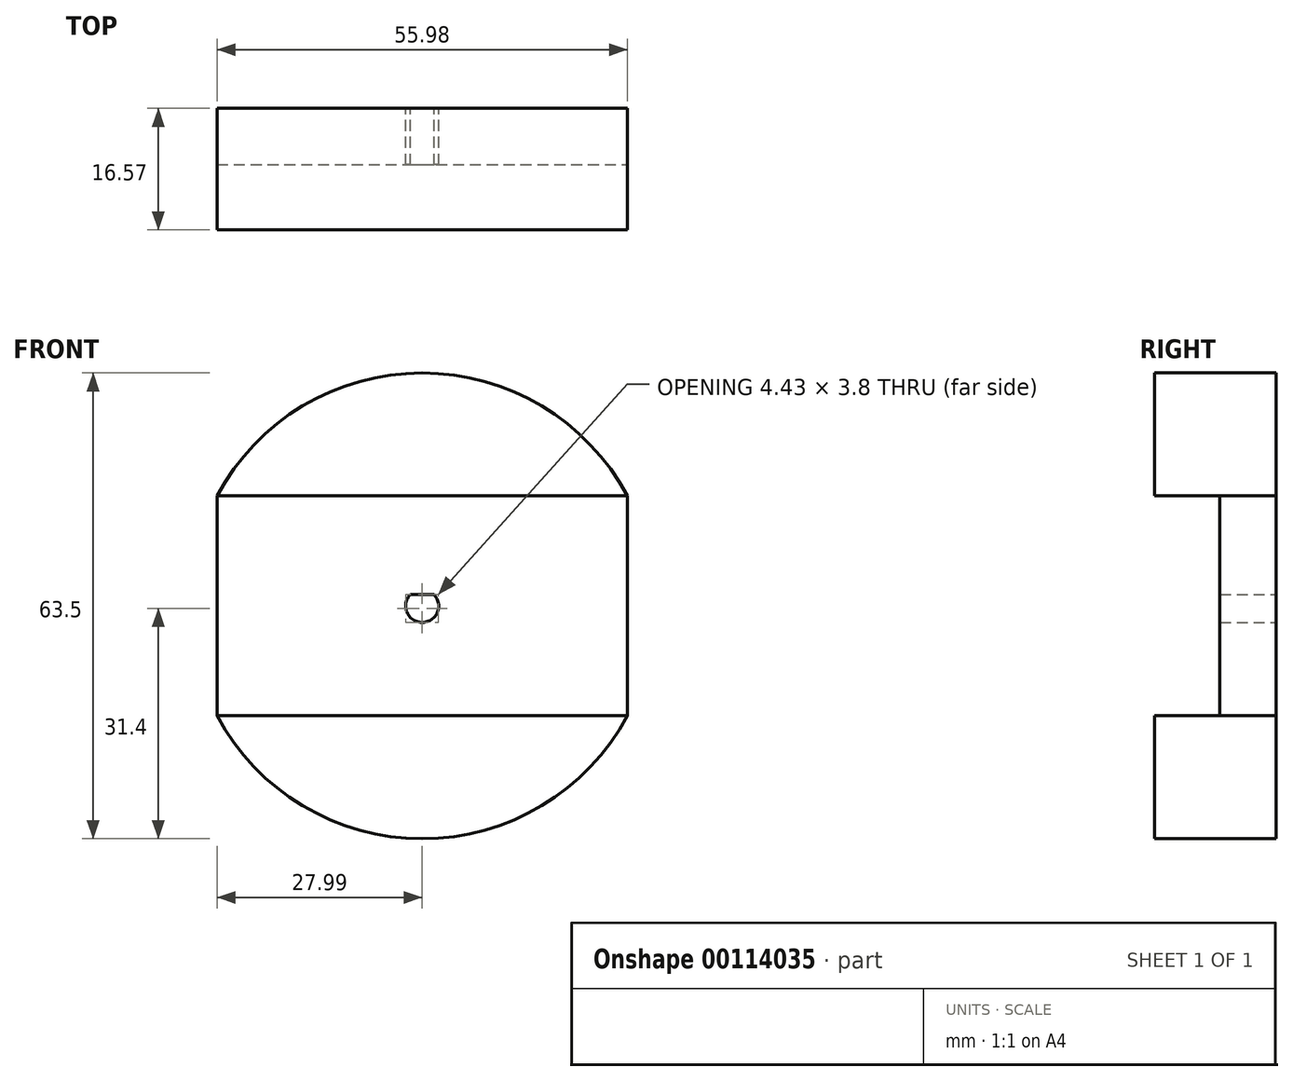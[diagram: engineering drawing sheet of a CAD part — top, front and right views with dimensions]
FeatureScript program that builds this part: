
annotation { "Feature Type Name" : "Feature", "Feature Type Description" : "" }
export const myFeature = defineFeature(function(context is Context, id is Id, definition is map)
    precondition{}
    {
        {
            var Q0;
            Q0=qCreatedBy(makeId("Front.planeOp"),FACE);
            var sketch = newSketch(context, id + "F0", { "sketchPlane" : qUnion([Q0])});
            skCircle(sketch, "E0", {"center": v(0, 0) * mm, "radius": 31.75 * mm});
            skCircle(sketch, "E1", {"center": v(0, 0) * mm, "radius": 2.25 * mm});
            skSolve(sketch);
        }
        {
            var Q0;
            Q0 = qSketchRegion(id + "F0", true);
            extrude(context, id + "F1", {"entities" : qUnion([Q0]), "depth" : 4 * mm});
        }
        {
            var Q0;
            Q0=makeQuery(id+"F1.opExtrude","CAP_FACE",FACE,{"disambiguationData":[OSD([sQuery(id+"F0.wireOp",EDGE,"E0"),sQuery(id+"F0.wireOp",EDGE,"E1")])],"isStart":false});
            var sketch = newSketch(context, id + "F2", { "sketchPlane" : qUnion([Q0])});
            skCircle(sketch, "E2", {"center": v(0, 0) * mm, "radius": 31.75 * mm});
            skLineSegment(sketch, "E3", {"start": v(-1.63, 1.55) * mm, "end": v(1.63, 1.55) * mm});
            skArc(sketch, "E4", {"start": v(1.63, 1.55) * mm, "mid": v(0, 2.25) * mm, "end": v(-1.63, 1.55) * mm});
            skSolve(sketch);
        }
        {
            var Q0;
            Q0=makeQuery(id+"F2.imprint","IMPRINT",FACE,{"disambiguationData":[TD([[makeQuery(id+"F2.imprint","IMPRINT",EDGE,{"derivedFrom":sQuery(id+"F2.wireOp",EDGE,"E2")}),1.0]])]});
            var Q1;
            Q1=makeQuery(id+"F2.imprint","IMPRINT",FACE,{"disambiguationData":[TD([[makeQuery(id+"F2.imprint","IMPRINT",EDGE,{"derivedFrom":sQuery(id+"F2.wireOp",EDGE,"E3")}),1.0]])]});
            extrude(context, id + "F3", {"entities" : qUnion([Q0, Q1]), "operationType" : NewBodyOperationType.ADD, "depth" : 8 * mm});
        }
        {
            var Q0;
            Q0=makeQuery(id+"F3.opExtrude","CAP_FACE",FACE,{"disambiguationData":[OSD([sQuery(id+"F0.wireOp",EDGE,"E1"),sQuery(id+"F2.wireOp",EDGE,"E2"),sQuery(id+"F2.wireOp",EDGE,"E3")])],"isStart":false});
            var sketch = newSketch(context, id + "F4", { "sketchPlane" : qUnion([Q0])});
            skLineSegment(sketch, "E5", {"start": v(-28, 14.99) * mm, "end": v(-28, -14.99) * mm});
            skLineSegment(sketch, "E6", {"start": v(28, 14.99) * mm, "end": v(28, -14.99) * mm});
            skLineSegment(sketch, "E7", {"start": v(-28, 14.99) * mm, "end": v(28, 14.99) * mm});
            skLineSegment(sketch, "E8", {"start": v(28, -14.99) * mm, "end": v(-28, -14.99) * mm});
            skSolve(sketch);
        }
        {
            var Q0;
            {var subQ0=sQuery(id+"F4.wireOp",EDGE,"E7");Q0=makeQuery(id+"F4.imprint","IMPRINT",FACE,{"disambiguationData":[TD([[makeQuery(id+"F4.imprint","IMPRINT",EDGE,{"derivedFrom":subQ0}),1.0]])]});}
            var Q1;
            {var subQ0=sQuery(id+"F4.wireOp",EDGE,"E8");Q1=makeQuery(id+"F4.imprint","IMPRINT",FACE,{"disambiguationData":[TD([[makeQuery(id+"F4.imprint","IMPRINT",EDGE,{"derivedFrom":subQ0}),1.0]])]});}
            extrude(context, id + "F5", {"entities" : qUnion([Q0, Q1]), "operationType" : NewBodyOperationType.ADD, "depth" : 8.9 * mm});
        }
        {
            var Q0;
            Q0=makeQuery(id+"F5.opExtrude","CAP_FACE",FACE,{"disambiguationData":[OSD([sQuery(id+"F2.wireOp",EDGE,"E2"),sQuery(id+"F4.wireOp",EDGE,"E7")])],"isStart":false});
            var sketch = newSketch(context, id + "F6", { "sketchPlane" : qUnion([Q0])});
            skCircle(sketch, "E9", {"center": v(0, 0) * mm, "radius": 31.75 * mm});
            skLineSegment(sketch, "E10", {"start": v(-28, 14.99) * mm, "end": v(-28, -14.99) * mm});
            skLineSegment(sketch, "E11", {"start": v(28, 14.99) * mm, "end": v(28, -14.99) * mm});
            skSolve(sketch);
        }
        {
            var Q0;
            {var subQ0=sQuery(id+"F6.wireOp",EDGE,"E10");Q0=makeQuery(id+"F6.imprint","IMPRINT",FACE,{"disambiguationData":[TD([[makeQuery(id+"F6.imprint","IMPRINT",EDGE,{"derivedFrom":subQ0}),-1.0]])]});}
            var Q1;
            {var subQ0=sQuery(id+"F6.wireOp",EDGE,"E11");Q1=makeQuery(id+"F6.imprint","IMPRINT",FACE,{"disambiguationData":[TD([[makeQuery(id+"F6.imprint","IMPRINT",EDGE,{"derivedFrom":subQ0}),1.0]])]});}
            extrude(context, id + "F7", {"entities" : qUnion([Q0, Q1]), "operationType" : NewBodyOperationType.REMOVE, "endBound" : BoundingType.THROUGH_ALL, "oppositeDirection" : true, "depth" : 25.4 * mm});
        }
        {
            var Q0;
            Q0=makeQuery(id+"F1.opExtrude","CAP_FACE",FACE,{"disambiguationData":[OSD([sQuery(id+"F0.wireOp",EDGE,"E0"),sQuery(id+"F0.wireOp",EDGE,"E1")])],"isStart":true});
            var sketch = newSketch(context, id + "F8", { "sketchPlane" : qUnion([Q0])});
            skCircle(sketch, "E12", {"center": v(0, 0) * mm, "radius": 39.7 * mm});
            skSolve(sketch);
        }
        {
            var Q0;
            Q0 = qSketchRegion(id + "F8", true);
            extrude(context, id + "F9", {"entities" : qUnion([Q0]), "operationType" : NewBodyOperationType.REMOVE, "oppositeDirection" : true, "depth" : 4.32 * mm});
        }
    });
